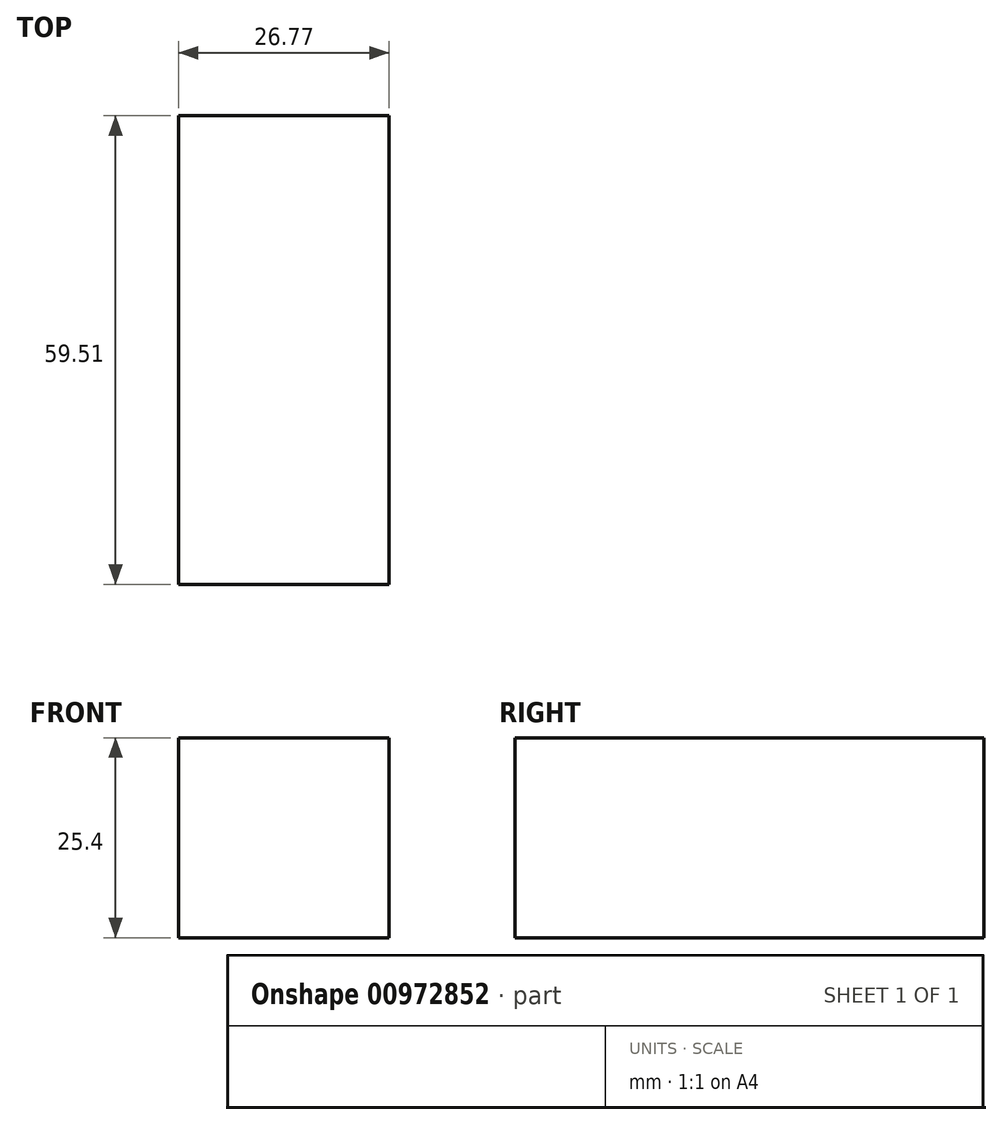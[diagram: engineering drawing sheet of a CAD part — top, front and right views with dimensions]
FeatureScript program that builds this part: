
annotation { "Feature Type Name" : "Feature", "Feature Type Description" : "" }
export const myFeature = defineFeature(function(context is Context, id is Id, definition is map)
    precondition{}
    {
        {
            var Q0;
            Q0=qCreatedBy(makeId("Top.planeOp"),FACE);
            var sketch = newSketch(context, id + "F0", { "sketchPlane" : qUnion([Q0])});
            skLineSegment(sketch, "E0.bottom", {"start": v(47.86, 0) * mm, "end": v(21.1, 0) * mm});
            skLineSegment(sketch, "E0.top", {"start": v(47.86, -59.5) * mm, "end": v(21.1, -59.5) * mm});
            skLineSegment(sketch, "E0.left", {"start": v(47.86, 0) * mm, "end": v(47.86, -59.5) * mm});
            skLineSegment(sketch, "E0.right", {"start": v(21.1, 0) * mm, "end": v(21.1, -59.5) * mm});
            skSolve(sketch);
        }
        {
            var Q0;
            Q0 = qSketchRegion(id + "F0", true);
            extrude(context, id + "F1", {"entities" : qUnion([Q0]), "depth" : 25.4 * mm, "offsetDistance" : 25.4 * mm});
        }
    });
